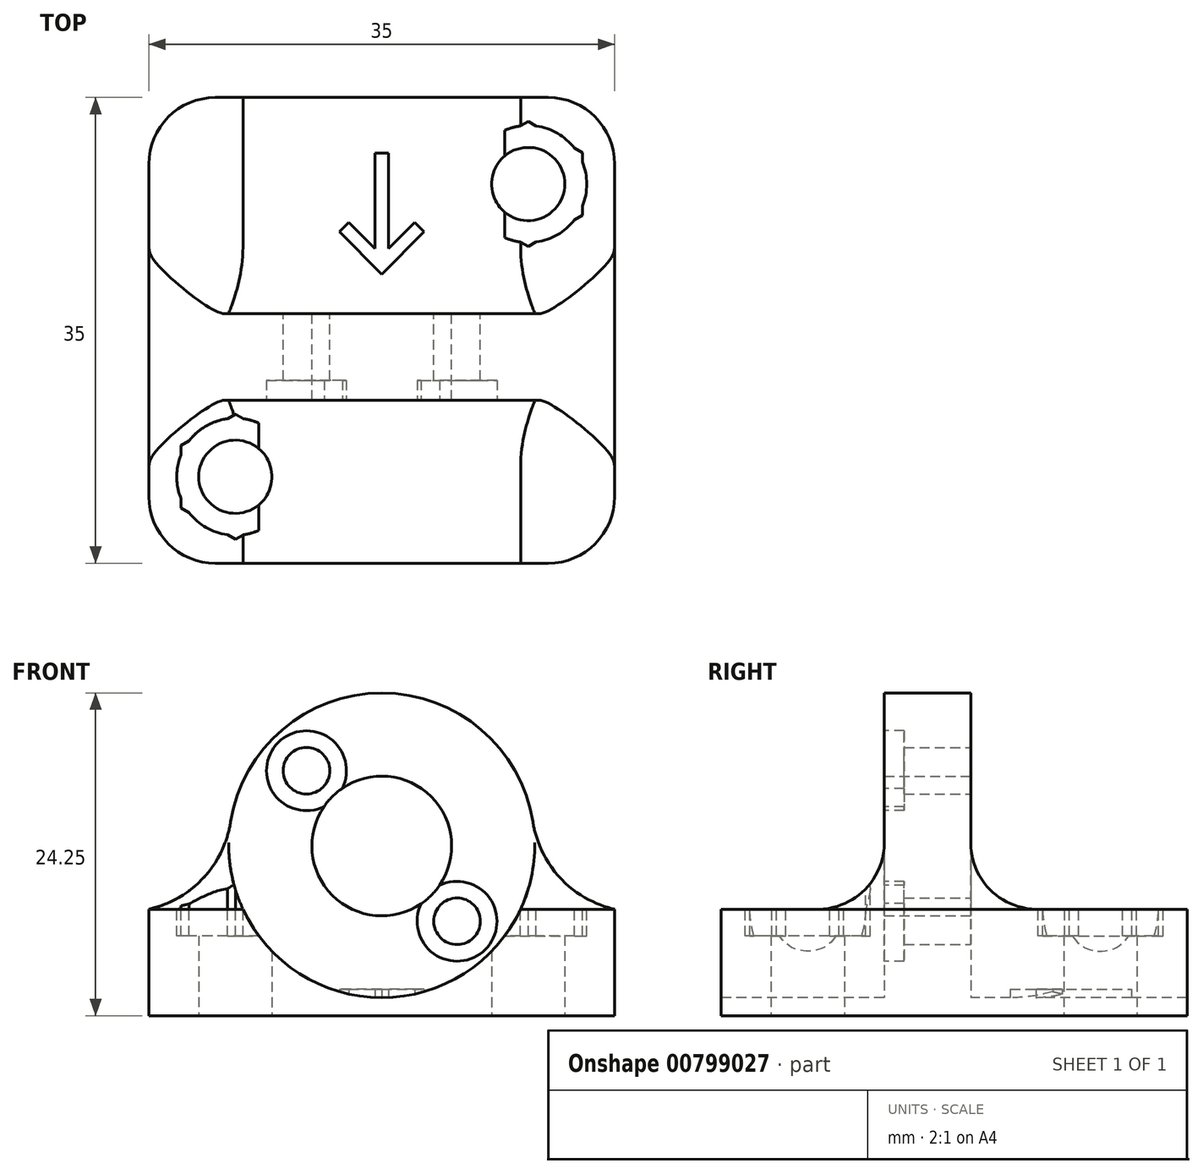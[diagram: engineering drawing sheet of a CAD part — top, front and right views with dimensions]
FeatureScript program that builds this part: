
annotation { "Feature Type Name" : "Feature", "Feature Type Description" : "" }
export const myFeature = defineFeature(function(context is Context, id is Id, definition is map)
    precondition{}
    {
        {
            var Q0;
            Q0=qCreatedBy(makeId("Front.planeOp"),FACE);
            cPlane(context, id + "F0", {"entities" : qUnion([Q0]), "cplaneType" : CPlaneType.OFFSET, "offset" : 2 * mm, "width" : 150 * mm, "height" : 150 * mm});
        }
        {
            var Q0;
            Q0=qCreatedBy(makeId("Top.planeOp"),FACE);
            var sketch = newSketch(context, id + "F1", { "sketchPlane" : qUnion([Q0])});
            skLineSegment(sketch, "E0.bottom", {"start": v(-17.5, 17.5) * mm, "end": v(17.5, 17.5) * mm});
            skLineSegment(sketch, "E0.top", {"start": v(-17.5, -17.5) * mm, "end": v(17.5, -17.5) * mm});
            skLineSegment(sketch, "E0.left", {"start": v(-17.5, 17.5) * mm, "end": v(-17.5, -17.5) * mm});
            skLineSegment(sketch, "E0.right", {"start": v(17.5, 17.5) * mm, "end": v(17.5, -17.5) * mm});
            skPoint(sketch, "E0.middle", {"position": v(0, 0) * mm});
            skLineSegment(sketch, "E1.bottom", {"start": v(-11, 11) * mm, "end": v(11, 11) * mm, "construction": true});
            skLineSegment(sketch, "E1.top", {"start": v(-11, -11) * mm, "end": v(11, -11) * mm, "construction": true});
            skLineSegment(sketch, "E1.left", {"start": v(-11, 11) * mm, "end": v(-11, -11) * mm, "construction": true});
            skLineSegment(sketch, "E1.right", {"start": v(11, 11) * mm, "end": v(11, -11) * mm, "construction": true});
            skCircle(sketch, "E2", {"center": v(-11, 11) * mm, "radius": 2.75 * mm, "construction": true});
            skCircle(sketch, "E3", {"center": v(11, 11) * mm, "radius": 2.75 * mm});
            skCircle(sketch, "E4", {"center": v(11, -11) * mm, "radius": 2.75 * mm, "construction": true});
            skCircle(sketch, "E5", {"center": v(-11, -11) * mm, "radius": 2.75 * mm});
            skSolve(sketch);
        }
        {
            var Q0;
            Q0=qSketchRegion(id+"F1",true);
            extrude(context, id + "F2", {"entities" : qUnion([Q0]), "depth" : 8 * mm, "offsetDistance" : 25 * mm});
        }
        {
            var Q0;
            Q0=qCreatedBy(id+"F0.planeOp",FACE);
            var sketch = newSketch(context, id + "F3", { "sketchPlane" : qUnion([Q0])});
            skLineSegment(sketch, "E6", {"start": v(0, 0) * mm, "end": v(0, 12.75) * mm, "construction": true});
            skArc(sketch, "E7", {"start": v(11.5, 12.75) * mm, "mid": v(0, 24.25) * mm, "end": v(-11.5, 12.75) * mm});
            skLineSegment(sketch, "E8", {"start": v(-11.5, 12.75) * mm, "end": v(-11.5, 0) * mm});
            skLineSegment(sketch, "E9.MirrorCS", {"start": v(11.5, 12.75) * mm, "end": v(11.5, 0) * mm});
            skCircle(sketch, "E10", {"center": v(0, 12.75) * mm, "radius": 5.25 * mm});
            skCircle(sketch, "E11", {"center": v(0, 12.75) * mm, "radius": 8 * mm, "construction": true});
            skLineSegment(sketch, "E12", {"start": v(0, 20.75) * mm, "end": v(0, 4.75) * mm, "construction": true});
            skPoint(sketch, "E12.startSnap0", {"position": v(0, 24.25) * mm});
            skLineSegment(sketch, "E13", {"start": v(-8, 12.75) * mm, "end": v(8, 12.75) * mm, "construction": true});
            skLineSegment(sketch, "E14", {"start": v(0, 12.75) * mm, "end": v(-5.66, 18.4) * mm, "construction": true});
            skLineSegment(sketch, "E15", {"start": v(0, 12.75) * mm, "end": v(-5.66, 7.1) * mm, "construction": true});
            skLineSegment(sketch, "E16.MirrorCS", {"start": v(0, 12.75) * mm, "end": v(5.66, 18.4) * mm, "construction": true});
            skLineSegment(sketch, "E17.MirrorCS", {"start": v(0, 12.75) * mm, "end": v(5.66, 7.1) * mm, "construction": true});
            skCircle(sketch, "E18", {"center": v(-5.66, 18.4) * mm, "radius": 1.75 * mm});
            skCircle(sketch, "E19", {"center": v(-5.66, 7.1) * mm, "radius": 1.75 * mm, "construction": true});
            skCircle(sketch, "E20", {"center": v(5.66, 7.1) * mm, "radius": 1.75 * mm});
            skCircle(sketch, "E21", {"center": v(5.66, 18.4) * mm, "radius": 1.75 * mm, "construction": true});
            skLineSegment(sketch, "E22", {"start": v(-11.5, 0) * mm, "end": v(11.5, 0) * mm});
            skSolve(sketch);
        }
        {
            var Q0;
            Q0=qCreatedBy(makeId("Front.planeOp"),FACE);
            var sketch = newSketch(context, id + "F4", { "sketchPlane" : qUnion([Q0])});
            skLineSegment(sketch, "E23", {"start": v(0, 0) * mm, "end": v(0, 12.85) * mm, "construction": true});
            skCircle(sketch, "E24", {"center": v(0, 12.85) * mm, "radius": 11.5 * mm});
            skSolve(sketch);
        }
        {
            var Q0;
            Q0=qSketchRegion(id+"F4",true);
            extrude(context, id + "F5", {"entities" : qUnion([Q0]), "operationType" : NewBodyOperationType.REMOVE, "endBound" : BoundingType.SYMMETRIC, "oppositeDirection" : true, "depth" : 36 * mm, "offsetDistance" : 25 * mm});
        }
        {
            var Q0;
            Q0=qSketchRegion(id+"F3",true);
            extrude(context, id + "F6", {"entities" : qUnion([Q0]), "operationType" : NewBodyOperationType.ADD, "endBound" : BoundingType.SYMMETRIC, "depth" : 6.5 * mm, "offsetDistance" : 25 * mm});
        }
        {
            var Q0;
            {var subQ0=sQuery(id+"F1.wireOp",EDGE,"E4");var subQ1=sQuery(id+"F1.wireOp",EDGE,"E0.top");var subQ2=sQuery(id+"F1.wireOp",EDGE,"E0.right");var subQ3=sQuery(id+"F1.wireOp",EDGE,"E0.bottom");Q0=makeQuery(id+"F6.boolean.opBoolean","INTERSECT",EDGE,{"derivedFrom":[makeQuery(id+"F5.boolean.opBoolean","SPLIT",FACE,{"disambiguationData":[TD([makeQuery(id+"F2.opExtrude","SWEPT_FACE",FACE,{"disambiguationData":[OSD([subQ2])]})])],"derivedFrom":makeQuery(id+"F2.opExtrude","CAP_FACE",FACE,{"disambiguationData":[OSD([subQ3,subQ1,sQuery(id+"F1.wireOp",EDGE,"E0.left"),subQ2,sQuery(id+"F1.wireOp",EDGE,"E2"),subQ0])],"isStart":false})}),makeQuery(id+"F6.opExtrude","SWEPT_FACE",FACE,{"disambiguationData":[OSD([sQuery(id+"F3.wireOp",EDGE,"E9.MirrorCS")])]})]});}
            var Q1;
            {var subQ0=sQuery(id+"F1.wireOp",EDGE,"E2");var subQ1=sQuery(id+"F1.wireOp",EDGE,"E0.left");var subQ2=sQuery(id+"F1.wireOp",EDGE,"E0.top");var subQ3=sQuery(id+"F1.wireOp",EDGE,"E0.bottom");Q1=makeQuery(id+"F6.boolean.opBoolean","INTERSECT",EDGE,{"derivedFrom":[makeQuery(id+"F5.boolean.opBoolean","SPLIT",FACE,{"disambiguationData":[TD([makeQuery(id+"F2.opExtrude","SWEPT_FACE",FACE,{"disambiguationData":[OSD([subQ1])]})])],"derivedFrom":makeQuery(id+"F2.opExtrude","CAP_FACE",FACE,{"disambiguationData":[OSD([subQ3,subQ2,subQ1,sQuery(id+"F1.wireOp",EDGE,"E0.right"),subQ0,sQuery(id+"F1.wireOp",EDGE,"E4")])],"isStart":false})}),makeQuery(id+"F6.opExtrude","SWEPT_FACE",FACE,{"disambiguationData":[OSD([sQuery(id+"F3.wireOp",EDGE,"E8")])]})]});}
            fillet(context, id + "F7", {"entities" : qUnion([Q0, Q1]), "radius" : 8 * mm, "tangentPropagation" : true, "allowEdgeOverflow" : false});
        }
        {
            var Q0;
            {var subQ0=sQuery(id+"F1.wireOp",EDGE,"E2");var subQ1=sQuery(id+"F1.wireOp",EDGE,"E0.left");var subQ2=sQuery(id+"F1.wireOp",EDGE,"E0.top");var subQ3=sQuery(id+"F1.wireOp",EDGE,"E0.bottom");Q0=makeQuery(id+"F7.opFillet","SPLIT",FACE,{"disambiguationData":[OD(0.0)],"derivedFrom":makeQuery(id+"F5.boolean.opBoolean","SPLIT",FACE,{"disambiguationData":[TD([makeQuery(id+"F2.opExtrude","SWEPT_FACE",FACE,{"disambiguationData":[OSD([subQ1])]})])],"derivedFrom":makeQuery(id+"F2.opExtrude","CAP_FACE",FACE,{"disambiguationData":[OSD([subQ3,subQ2,subQ1,sQuery(id+"F1.wireOp",EDGE,"E0.right"),subQ0,sQuery(id+"F1.wireOp",EDGE,"E4")])],"isStart":false})})});}
            var sketch = newSketch(context, id + "F8", { "sketchPlane" : qUnion([Q0])});
            skPoint(sketch, "E25.0.midPoint.positionSnap0", {"position": v(5.2, -11) * mm});
            skLineSegment(sketch, "E26", {"start": v(17.5, 17.5) * mm, "end": v(-17.5, -17.5) * mm, "construction": true});
            skCircle(sketch, "E27.cCircle", {"center": v(11, 11) * mm, "radius": 4.08 * mm, "construction": true});
            skLineSegment(sketch, "E27.0", {"start": v(15.08, 13.35) * mm, "end": v(15.07, 8.65) * mm});
            skLineSegment(sketch, "E27.1", {"start": v(15.07, 8.65) * mm, "end": v(11, 6.3) * mm});
            skLineSegment(sketch, "E27.2", {"start": v(11, 6.3) * mm, "end": v(6.93, 8.65) * mm});
            skLineSegment(sketch, "E27.3", {"start": v(6.93, 8.65) * mm, "end": v(6.93, 13.35) * mm});
            skLineSegment(sketch, "E27.4", {"start": v(6.93, 13.35) * mm, "end": v(11, 15.7) * mm});
            skLineSegment(sketch, "E27.5", {"start": v(11, 15.7) * mm, "end": v(15.07, 13.35) * mm});
            skPoint(sketch, "E27.0.midPoint", {"position": v(15.08, 11) * mm});
            skCircle(sketch, "E28.cCircle", {"center": v(-11, -11) * mm, "radius": 4.08 * mm, "construction": true});
            skLineSegment(sketch, "E28.0", {"start": v(-11, -6.3) * mm, "end": v(-6.93, -8.65) * mm});
            skLineSegment(sketch, "E28.1", {"start": v(-6.93, -8.65) * mm, "end": v(-6.93, -13.35) * mm});
            skLineSegment(sketch, "E28.2", {"start": v(-6.93, -13.35) * mm, "end": v(-11, -15.7) * mm});
            skLineSegment(sketch, "E28.3", {"start": v(-11, -15.7) * mm, "end": v(-15.08, -13.35) * mm});
            skLineSegment(sketch, "E28.4", {"start": v(-15.07, -13.35) * mm, "end": v(-15.07, -8.65) * mm});
            skLineSegment(sketch, "E28.5", {"start": v(-15.07, -8.65) * mm, "end": v(-11, -6.3) * mm});
            skPoint(sketch, "E28.0.midPoint", {"position": v(-8.96, -7.47) * mm});
            skSolve(sketch);
        }
        {
            var Q0;
            Q0=qSketchRegion(id+"F8",true);
            extrude(context, id + "F9", {"entities" : qUnion([Q0]), "operationType" : NewBodyOperationType.REMOVE, "oppositeDirection" : true, "depth" : 2 * mm, "offsetDistance" : 25 * mm});
        }
        {
            var Q0;
            {var subQ0=sQuery(id+"F1.wireOp",EDGE,"E2");var subQ1=sQuery(id+"F1.wireOp",EDGE,"E0.left");var subQ2=sQuery(id+"F1.wireOp",EDGE,"E0.top");var subQ3=sQuery(id+"F1.wireOp",EDGE,"E0.bottom");Q0=makeQuery(id+"F7.opFillet","SPLIT",FACE,{"disambiguationData":[OD(0.0)],"derivedFrom":makeQuery(id+"F5.boolean.opBoolean","SPLIT",FACE,{"disambiguationData":[TD([makeQuery(id+"F2.opExtrude","SWEPT_FACE",FACE,{"disambiguationData":[OSD([subQ1])]})])],"derivedFrom":makeQuery(id+"F2.opExtrude","CAP_FACE",FACE,{"disambiguationData":[OSD([subQ3,subQ2,subQ1,sQuery(id+"F1.wireOp",EDGE,"E0.right"),subQ0,sQuery(id+"F1.wireOp",EDGE,"E4")])],"isStart":false})})});}
            var sketch = newSketch(context, id + "F10", { "sketchPlane" : qUnion([Q0])});
            skCircle(sketch, "E29", {"center": v(11, 11) * mm, "radius": 4.4 * mm});
            skCircle(sketch, "E30", {"center": v(-11, -11) * mm, "radius": 4.4 * mm});
            skSolve(sketch);
        }
        {
            var Q0;
            Q0=qSketchRegion(id+"F10",true);
            extrude(context, id + "F11", {"entities" : qUnion([Q0]), "operationType" : NewBodyOperationType.REMOVE, "oppositeDirection" : true, "depth" : 2 * mm, "offsetDistance" : 25 * mm});
        }
        {
            var Q0;
            {var subQ0=sQuery(id+"F1.wireOp",EDGE,"E4");var subQ1=sQuery(id+"F1.wireOp",EDGE,"E0.top");var subQ2=sQuery(id+"F1.wireOp",EDGE,"E0.right");var subQ3=sQuery(id+"F1.wireOp",EDGE,"E0.bottom");Q0=makeQuery(id+"F6.boolean.opBoolean","INTERSECT",EDGE,{"derivedFrom":[makeQuery(id+"F5.boolean.opBoolean","SPLIT",FACE,{"disambiguationData":[TD([makeQuery(id+"F2.opExtrude","SWEPT_FACE",FACE,{"disambiguationData":[OSD([subQ2])]})])],"derivedFrom":makeQuery(id+"F2.opExtrude","CAP_FACE",FACE,{"disambiguationData":[OSD([subQ3,subQ1,sQuery(id+"F1.wireOp",EDGE,"E0.left"),subQ2,sQuery(id+"F1.wireOp",EDGE,"E2"),subQ0])],"isStart":false})}),makeQuery(id+"F6.opExtrude","CAP_FACE",FACE,{"disambiguationData":[OSD([sQuery(id+"F3.wireOp",EDGE,"E7"),sQuery(id+"F3.wireOp",EDGE,"E8"),sQuery(id+"F3.wireOp",EDGE,"E9.MirrorCS"),sQuery(id+"F3.wireOp",EDGE,"E10"),sQuery(id+"F3.wireOp",EDGE,"E18"),sQuery(id+"F3.wireOp",EDGE,"E19"),sQuery(id+"F3.wireOp",EDGE,"E20"),sQuery(id+"F3.wireOp",EDGE,"E21"),sQuery(id+"F3.wireOp",EDGE,"E22")])],"isStart":true})]});}
            var Q1;
            {var subQ0=sQuery(id+"F1.wireOp",EDGE,"E2");var subQ1=sQuery(id+"F1.wireOp",EDGE,"E0.left");var subQ2=sQuery(id+"F1.wireOp",EDGE,"E0.top");var subQ3=sQuery(id+"F1.wireOp",EDGE,"E0.bottom");Q1=makeQuery(id+"F6.boolean.opBoolean","INTERSECT",EDGE,{"derivedFrom":[makeQuery(id+"F5.boolean.opBoolean","SPLIT",FACE,{"disambiguationData":[TD([makeQuery(id+"F2.opExtrude","SWEPT_FACE",FACE,{"disambiguationData":[OSD([subQ1])]})])],"derivedFrom":makeQuery(id+"F2.opExtrude","CAP_FACE",FACE,{"disambiguationData":[OSD([subQ3,subQ2,subQ1,sQuery(id+"F1.wireOp",EDGE,"E0.right"),subQ0,sQuery(id+"F1.wireOp",EDGE,"E4")])],"isStart":false})}),makeQuery(id+"F6.opExtrude","CAP_FACE",FACE,{"disambiguationData":[OSD([sQuery(id+"F3.wireOp",EDGE,"E7"),sQuery(id+"F3.wireOp",EDGE,"E8"),sQuery(id+"F3.wireOp",EDGE,"E9.MirrorCS"),sQuery(id+"F3.wireOp",EDGE,"E10"),sQuery(id+"F3.wireOp",EDGE,"E18"),sQuery(id+"F3.wireOp",EDGE,"E19"),sQuery(id+"F3.wireOp",EDGE,"E20"),sQuery(id+"F3.wireOp",EDGE,"E21"),sQuery(id+"F3.wireOp",EDGE,"E22")])],"isStart":true})]});}
            var Q2;
            {var subQ0=sQuery(id+"F1.wireOp",EDGE,"E2");var subQ1=sQuery(id+"F1.wireOp",EDGE,"E0.left");var subQ2=sQuery(id+"F1.wireOp",EDGE,"E0.top");var subQ3=sQuery(id+"F1.wireOp",EDGE,"E0.bottom");Q2=makeQuery(id+"F6.boolean.opBoolean","INTERSECT",EDGE,{"derivedFrom":[makeQuery(id+"F5.boolean.opBoolean","SPLIT",FACE,{"disambiguationData":[TD([makeQuery(id+"F2.opExtrude","SWEPT_FACE",FACE,{"disambiguationData":[OSD([subQ1])]})])],"derivedFrom":makeQuery(id+"F2.opExtrude","CAP_FACE",FACE,{"disambiguationData":[OSD([subQ3,subQ2,subQ1,sQuery(id+"F1.wireOp",EDGE,"E0.right"),subQ0,sQuery(id+"F1.wireOp",EDGE,"E4")])],"isStart":false})}),makeQuery(id+"F6.opExtrude","CAP_FACE",FACE,{"disambiguationData":[OSD([sQuery(id+"F3.wireOp",EDGE,"E7"),sQuery(id+"F3.wireOp",EDGE,"E8"),sQuery(id+"F3.wireOp",EDGE,"E9.MirrorCS"),sQuery(id+"F3.wireOp",EDGE,"E10"),sQuery(id+"F3.wireOp",EDGE,"E18"),sQuery(id+"F3.wireOp",EDGE,"E19"),sQuery(id+"F3.wireOp",EDGE,"E20"),sQuery(id+"F3.wireOp",EDGE,"E21"),sQuery(id+"F3.wireOp",EDGE,"E22")])],"isStart":false})]});}
            var Q3;
            {var subQ0=sQuery(id+"F1.wireOp",EDGE,"E4");var subQ1=sQuery(id+"F1.wireOp",EDGE,"E0.top");var subQ2=sQuery(id+"F1.wireOp",EDGE,"E0.right");var subQ3=sQuery(id+"F1.wireOp",EDGE,"E0.bottom");Q3=makeQuery(id+"F6.boolean.opBoolean","INTERSECT",EDGE,{"derivedFrom":[makeQuery(id+"F5.boolean.opBoolean","SPLIT",FACE,{"disambiguationData":[TD([makeQuery(id+"F2.opExtrude","SWEPT_FACE",FACE,{"disambiguationData":[OSD([subQ2])]})])],"derivedFrom":makeQuery(id+"F2.opExtrude","CAP_FACE",FACE,{"disambiguationData":[OSD([subQ3,subQ1,sQuery(id+"F1.wireOp",EDGE,"E0.left"),subQ2,sQuery(id+"F1.wireOp",EDGE,"E2"),subQ0])],"isStart":false})}),makeQuery(id+"F6.opExtrude","CAP_FACE",FACE,{"disambiguationData":[OSD([sQuery(id+"F3.wireOp",EDGE,"E7"),sQuery(id+"F3.wireOp",EDGE,"E8"),sQuery(id+"F3.wireOp",EDGE,"E9.MirrorCS"),sQuery(id+"F3.wireOp",EDGE,"E10"),sQuery(id+"F3.wireOp",EDGE,"E18"),sQuery(id+"F3.wireOp",EDGE,"E19"),sQuery(id+"F3.wireOp",EDGE,"E20"),sQuery(id+"F3.wireOp",EDGE,"E21"),sQuery(id+"F3.wireOp",EDGE,"E22")])],"isStart":false})]});}
            var Q4;
            Q4=makeQuery(id+"F2.opExtrude","SWEPT_EDGE",EDGE,{"disambiguationData":[OSD([sQuery(id+"F1.wireOp",EDGE,"E0.top"),sQuery(id+"F1.wireOp",EDGE,"E0.left")])]});
            var Q5;
            Q5=makeQuery(id+"F2.opExtrude","SWEPT_EDGE",EDGE,{"disambiguationData":[OSD([sQuery(id+"F1.wireOp",EDGE,"E0.bottom"),sQuery(id+"F1.wireOp",EDGE,"E0.left")])]});
            var Q6;
            Q6=makeQuery(id+"F2.opExtrude","SWEPT_EDGE",EDGE,{"disambiguationData":[OSD([sQuery(id+"F1.wireOp",EDGE,"E0.bottom"),sQuery(id+"F1.wireOp",EDGE,"E0.right")])]});
            var Q7;
            Q7=makeQuery(id+"F2.opExtrude","SWEPT_EDGE",EDGE,{"disambiguationData":[OSD([sQuery(id+"F1.wireOp",EDGE,"E0.top"),sQuery(id+"F1.wireOp",EDGE,"E0.right")])]});
            fillet(context, id + "F12", {"entities" : qUnion([Q0, Q1, Q2, Q3, Q4, Q5, Q6, Q7]), "radius" : 5 * mm, "tangentPropagation" : true, "allowEdgeOverflow" : false});
        }
        {
            var Q0;
            Q0=makeQuery(id+"F6.opExtrude","CAP_FACE",FACE,{"disambiguationData":[OSD([sQuery(id+"F3.wireOp",EDGE,"E7"),sQuery(id+"F3.wireOp",EDGE,"E8"),sQuery(id+"F3.wireOp",EDGE,"E9.MirrorCS"),sQuery(id+"F3.wireOp",EDGE,"E10"),sQuery(id+"F3.wireOp",EDGE,"E18"),sQuery(id+"F3.wireOp",EDGE,"E20"),sQuery(id+"F3.wireOp",EDGE,"E22")])],"isStart":false});
            var sketch = newSketch(context, id + "F13", { "sketchPlane" : qUnion([Q0])});
            skCircle(sketch, "E31", {"center": v(-5.66, 18.4) * mm, "radius": 3 * mm});
            skCircle(sketch, "E32", {"center": v(5.66, 7.1) * mm, "radius": 3 * mm});
            skSolve(sketch);
        }
        {
            var Q0;
            Q0=makeQuery(id+"F13.imprint","IMPRINT",FACE,{"disambiguationData":[TD([[makeQuery(id+"F13.imprint","IMPRINT",EDGE,{"derivedFrom":sQuery(id+"F13.wireOp",EDGE,"E31")}),1.0]])]});
            var Q1;
            Q1=makeQuery(id+"F13.imprint","IMPRINT",FACE,{"disambiguationData":[TD([[makeQuery(id+"F13.imprint","IMPRINT",EDGE,{"derivedFrom":sQuery(id+"F13.wireOp",EDGE,"E32")}),1.0]])]});
            var Q2;
            Q2=makeQuery(id+"F13.imprint","IMPRINT",FACE,{"disambiguationData":[TD([[makeQuery(id+"F13.imprint","IMPRINT",EDGE,{"derivedFrom":makeQuery(id+"F6.opExtrude","CAP_EDGE",EDGE,{"disambiguationData":[OSD([sQuery(id+"F3.wireOp",EDGE,"E18")])],"isStart":false})}),-1.0]])]});
            var Q3;
            Q3=makeQuery(id+"F13.imprint","IMPRINT",FACE,{"disambiguationData":[TD([[makeQuery(id+"F13.imprint","IMPRINT",EDGE,{"derivedFrom":makeQuery(id+"F6.opExtrude","CAP_EDGE",EDGE,{"disambiguationData":[OSD([sQuery(id+"F3.wireOp",EDGE,"E20")])],"isStart":false})}),-1.0]])]});
            var Q4;
            Q4=makeQuery(id+"F6.opExtrude","CAP_FACE",FACE,{"disambiguationData":[OSD([sQuery(id+"F3.wireOp",EDGE,"E7"),sQuery(id+"F3.wireOp",EDGE,"E8"),sQuery(id+"F3.wireOp",EDGE,"E9.MirrorCS"),sQuery(id+"F3.wireOp",EDGE,"E10"),sQuery(id+"F3.wireOp",EDGE,"E18"),sQuery(id+"F3.wireOp",EDGE,"E20"),sQuery(id+"F3.wireOp",EDGE,"E22")])],"isStart":true});
            extrude(context, id + "F14", {"entities" : qUnion([Q0, Q1, Q2, Q3]), "operationType" : NewBodyOperationType.REMOVE, "oppositeDirection" : true, "depth" : 1.5 * mm, "endBoundEntityFace" : qUnion([Q4]), "hasOffset" : true, "offsetDistance" : 5 * mm, "offsetOppositeDirection" : true});
        }
        {
            var Q0;
            Q0=makeQuery(id+"F2.opExtrude","CAP_FACE",FACE,{"disambiguationData":[OSD([sQuery(id+"F1.wireOp",EDGE,"E0.bottom"),sQuery(id+"F1.wireOp",EDGE,"E0.top"),sQuery(id+"F1.wireOp",EDGE,"E0.left"),sQuery(id+"F1.wireOp",EDGE,"E0.right"),sQuery(id+"F1.wireOp",EDGE,"E3"),sQuery(id+"F1.wireOp",EDGE,"E5")])],"isStart":true});
            var sketch = newSketch(context, id + "F15", { "sketchPlane" : qUnion([Q0])});
            skLineSegment(sketch, "E33", {"start": v(0, 0) * mm, "end": v(0, -17.5) * mm, "construction": true});
            skLineSegment(sketch, "E34", {"start": v(0, -4.22) * mm, "end": v(-3.18, -7.4) * mm});
            skLineSegment(sketch, "E35", {"start": v(-3.18, -7.4) * mm, "end": v(-2.47, -8.1) * mm});
            skLineSegment(sketch, "E36", {"start": v(-2.47, -8.1) * mm, "end": v(-0.5, -6.13) * mm});
            skLineSegment(sketch, "E37", {"start": v(-0.5, -6.13) * mm, "end": v(-0.5, -13.33) * mm});
            skLineSegment(sketch, "E38", {"start": v(-0.5, -13.33) * mm, "end": v(0, -13.33) * mm});
            skLineSegment(sketch, "E39.MirrorCS", {"start": v(0.5, -13.33) * mm, "end": v(0, -13.33) * mm});
            skLineSegment(sketch, "E40.MirrorCS", {"start": v(3.18, -7.4) * mm, "end": v(2.47, -8.1) * mm});
            skLineSegment(sketch, "E41.MirrorCS", {"start": v(0.5, -6.13) * mm, "end": v(0.5, -13.33) * mm});
            skLineSegment(sketch, "E42.MirrorCS", {"start": v(2.47, -8.1) * mm, "end": v(0.5, -6.13) * mm});
            skLineSegment(sketch, "E43.MirrorCS", {"start": v(0, -4.22) * mm, "end": v(3.18, -7.4) * mm});
            skSolve(sketch);
        }
        {
            var Q0;
            Q0=qSketchRegion(id+"F15",true);
            extrude(context, id + "F16", {"entities" : qUnion([Q0]), "operationType" : NewBodyOperationType.ADD, "oppositeDirection" : true, "depth" : 2 * mm, "offsetDistance" : 25 * mm});
        }
    });
